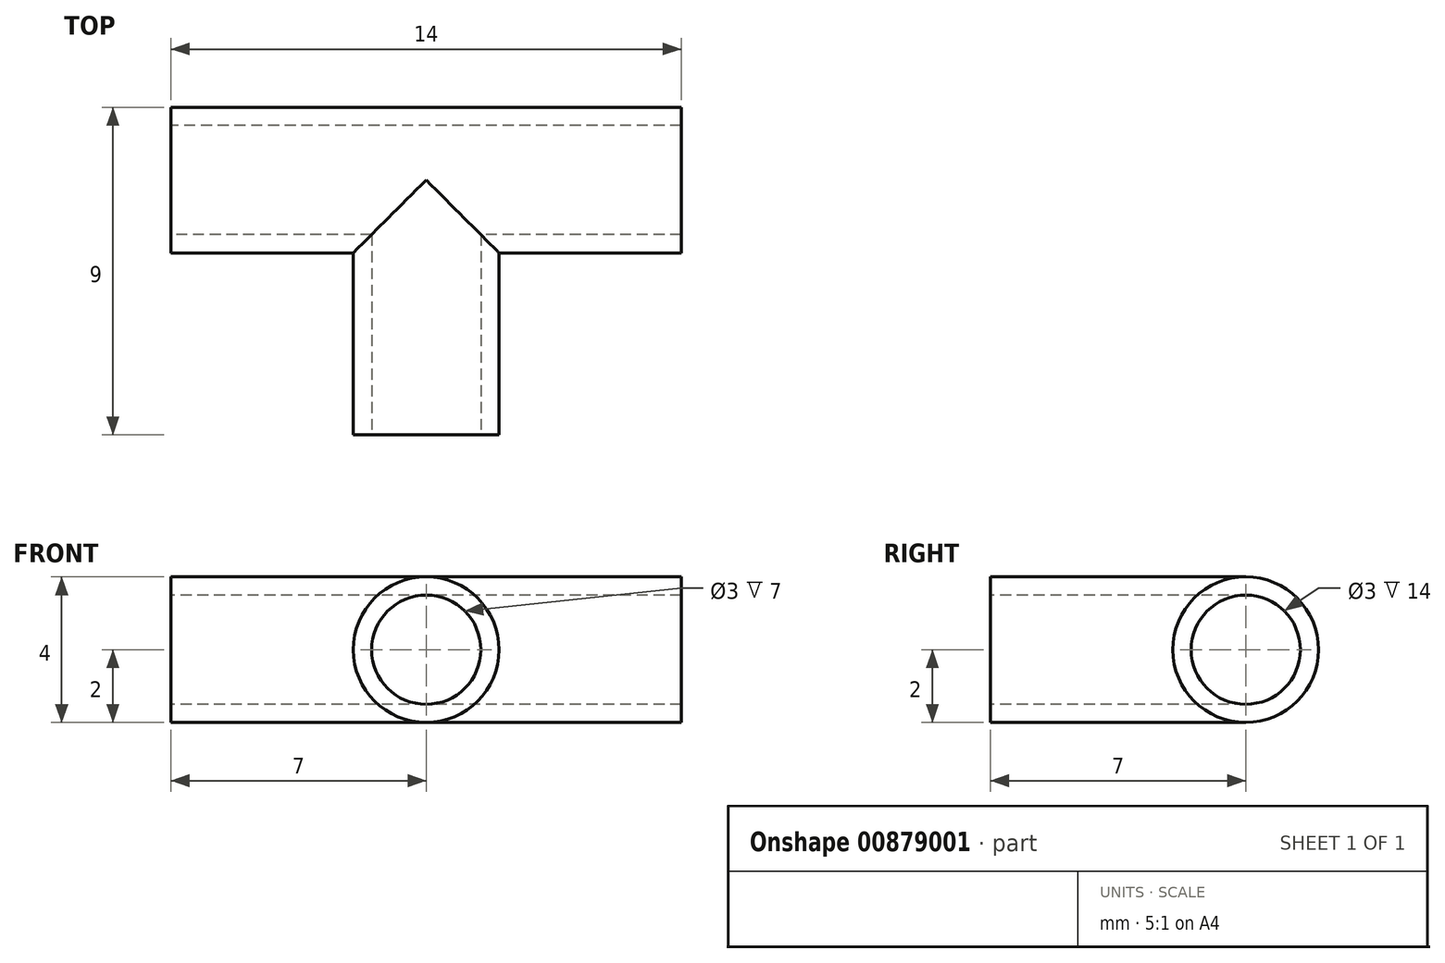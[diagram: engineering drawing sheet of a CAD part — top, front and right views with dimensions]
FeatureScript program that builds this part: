
annotation { "Feature Type Name" : "Feature", "Feature Type Description" : "" }
export const myFeature = defineFeature(function(context is Context, id is Id, definition is map)
    precondition{}
    {
        {
            var Q0;
            Q0=qCreatedBy(makeId("Front.planeOp"),FACE);
            var sketch = newSketch(context, id + "F0", { "sketchPlane" : qUnion([Q0])});
            skCircle(sketch, "E0", {"center": v(0, 0) * mm, "radius": 2 * mm});
            skCircle(sketch, "E1", {"center": v(0, 0) * mm, "radius": 1.5 * mm});
            skSolve(sketch);
        }
        {
            var Q0;
            Q0=qSketchRegion(id+"F0",true);
            extrude(context, id + "F1", {"entities" : qUnion([Q0]), "endBound" : BoundingType.SYMMETRIC, "depth" : 10 * mm, "offsetDistance" : 25 * mm});
        }
        {
            var Q0;
            Q0=qCreatedBy(makeId("Right.planeOp"),FACE);
            var sketch = newSketch(context, id + "F2", { "sketchPlane" : qUnion([Q0])});
            skCircle(sketch, "E2", {"center": v(0, 0) * mm, "radius": 1.5 * mm});
            skLineSegment(sketch, "E3", {"start": v(0, 0) * mm, "end": v(0, 5.43) * mm});
            skLineSegment(sketch, "E4", {"start": v(0, 0) * mm, "end": v(0, -2.3) * mm});
            skLineSegment(sketch, "E5", {"start": v(0, 2.48) * mm, "end": v(-6.1, 2.48) * mm});
            skLineSegment(sketch, "E6", {"start": v(-6.1, 2.48) * mm, "end": v(-6.1, -2.66) * mm});
            skLineSegment(sketch, "E7", {"start": v(-6.1, -2.66) * mm, "end": v(0, -2.66) * mm});
            skLineSegment(sketch, "E8", {"start": v(0, -2.66) * mm, "end": v(0, -2.3) * mm});
            skArc(sketch, "E9", {"start": v(0, -2) * mm, "mid": v(2, 0) * mm, "end": v(0, 2) * mm});
            skSolve(sketch);
        }
        {
            var Q0;
            {var subQ5=sQuery(id+"F2.wireOp",EDGE,"E5");Q0=makeQuery(id+"F2.imprint","IMPRINT",FACE,{"disambiguationData":[TD([[makeQuery(id+"F2.imprint","IMPRINT",EDGE,{"derivedFrom":subQ5}),1.0]])]});}
            var Q1;
            {var subQ0=sQuery(id+"F2.wireOp",EDGE,"E3");var subQ1=sQuery(id+"F2.wireOp",EDGE,"E2");var subQ2=makeQuery(id+"F2.imprint","INTERSECT",VERTEX,{"derivedFrom":[subQ1,subQ0]});Q1=makeQuery(id+"F2.imprint","IMPRINT",FACE,{"disambiguationData":[TD([[makeQuery(id+"F2.imprint","IMPRINT",EDGE,{"disambiguationData":[TD([[subQ2,-1.0]])],"derivedFrom":subQ1}),1.0]])]});}
            var Q2;
            {var subQ0=sQuery(id+"F2.wireOp",EDGE,"E3");var subQ1=sQuery(id+"F2.wireOp",EDGE,"E2");var subQ2=makeQuery(id+"F2.imprint","INTERSECT",VERTEX,{"derivedFrom":[subQ1,subQ0]});Q2=makeQuery(id+"F2.imprint","IMPRINT",FACE,{"disambiguationData":[TD([[makeQuery(id+"F2.imprint","IMPRINT",EDGE,{"disambiguationData":[TD([[subQ2,1.0]])],"derivedFrom":subQ1}),1.0]])]});}
            extrude(context, id + "F3", {"entities" : qUnion([Q0, Q1, Q2]), "operationType" : NewBodyOperationType.REMOVE, "endBound" : BoundingType.SYMMETRIC, "depth" : 25 * mm, "offsetDistance" : 25 * mm});
        }
        {
            var Q0;
            Q0=makeQuery(id+"F3.boolean.opBoolean","SPLIT",BODY,{"disambiguationData":[OD(0.0)],"derivedFrom":makeQuery(id+"F1.opExtrude","SWEPT_BODY",BODY,{"disambiguationData":[OSD([sQuery(id+"F0.wireOp",EDGE,"E0"),sQuery(id+"F0.wireOp",EDGE,"E1")])]})});
            var Q1;
            Q1=sQuery(id+"F2.wireOp",EDGE,"E3");
            circularPattern(context, id + "F4", {"entities" : qUnion([Q0]), "axis" : qUnion([Q1]), "angle" : 360 * degree, "instanceCount" : 4, "equalSpace" : true});
        }
        {
            var Q0;
            Q0=makeQuery(id+"F4.opPattern","COPY",FACE,{"derivedFrom":makeQuery(id+"F1.opExtrude","CAP_FACE",FACE,{"disambiguationData":[OSD([sQuery(id+"F0.wireOp",EDGE,"E0"),sQuery(id+"F0.wireOp",EDGE,"E1")])],"isStart":true}),"instanceName":"1"});
            extrude(context, id + "F5", {"entities" : qUnion([Q0]), "operationType" : NewBodyOperationType.ADD, "depth" : 2 * mm, "offsetDistance" : 25 * mm});
        }
        {
            var Q0;
            Q0=makeQuery(id+"F4.opPattern","COPY",FACE,{"derivedFrom":makeQuery(id+"F1.opExtrude","CAP_FACE",FACE,{"disambiguationData":[OSD([sQuery(id+"F0.wireOp",EDGE,"E0"),sQuery(id+"F0.wireOp",EDGE,"E1")])],"isStart":true}),"instanceName":"2"});
            extrude(context, id + "F6", {"entities" : qUnion([Q0]), "operationType" : NewBodyOperationType.ADD, "depth" : 2 * mm, "offsetDistance" : 25 * mm});
        }
        {
            var Q0;
            Q0=makeQuery(id+"F4.opPattern","COPY",FACE,{"derivedFrom":makeQuery(id+"F1.opExtrude","CAP_FACE",FACE,{"disambiguationData":[OSD([sQuery(id+"F0.wireOp",EDGE,"E0"),sQuery(id+"F0.wireOp",EDGE,"E1")])],"isStart":true}),"instanceName":"3"});
            extrude(context, id + "F7", {"entities" : qUnion([Q0]), "operationType" : NewBodyOperationType.ADD, "depth" : 2 * mm, "offsetDistance" : 25 * mm});
        }
        {
            var Q0;
            Q0=makeQuery(id+"F1.opExtrude","SWEPT_BODY",BODY,{"disambiguationData":[OSD([sQuery(id+"F0.wireOp",EDGE,"E0"),sQuery(id+"F0.wireOp",EDGE,"E1")])]});
            deleteBodies(context, id + "F8", {"entities" : qUnion([Q0])});
        }
        {
            var Q0;
            {var subQ5=sQuery(id+"F2.wireOp",EDGE,"E9");Q0=makeQuery(id+"F2.imprint","IMPRINT",FACE,{"disambiguationData":[TD([[makeQuery(id+"F2.imprint","IMPRINT",EDGE,{"derivedFrom":subQ5}),1.0]])]});}
            extrude(context, id + "F9", {"entities" : qUnion([Q0]), "operationType" : NewBodyOperationType.ADD, "endBound" : BoundingType.SYMMETRIC, "depth" : 6 * mm, "offsetDistance" : 25 * mm});
        }
    });
